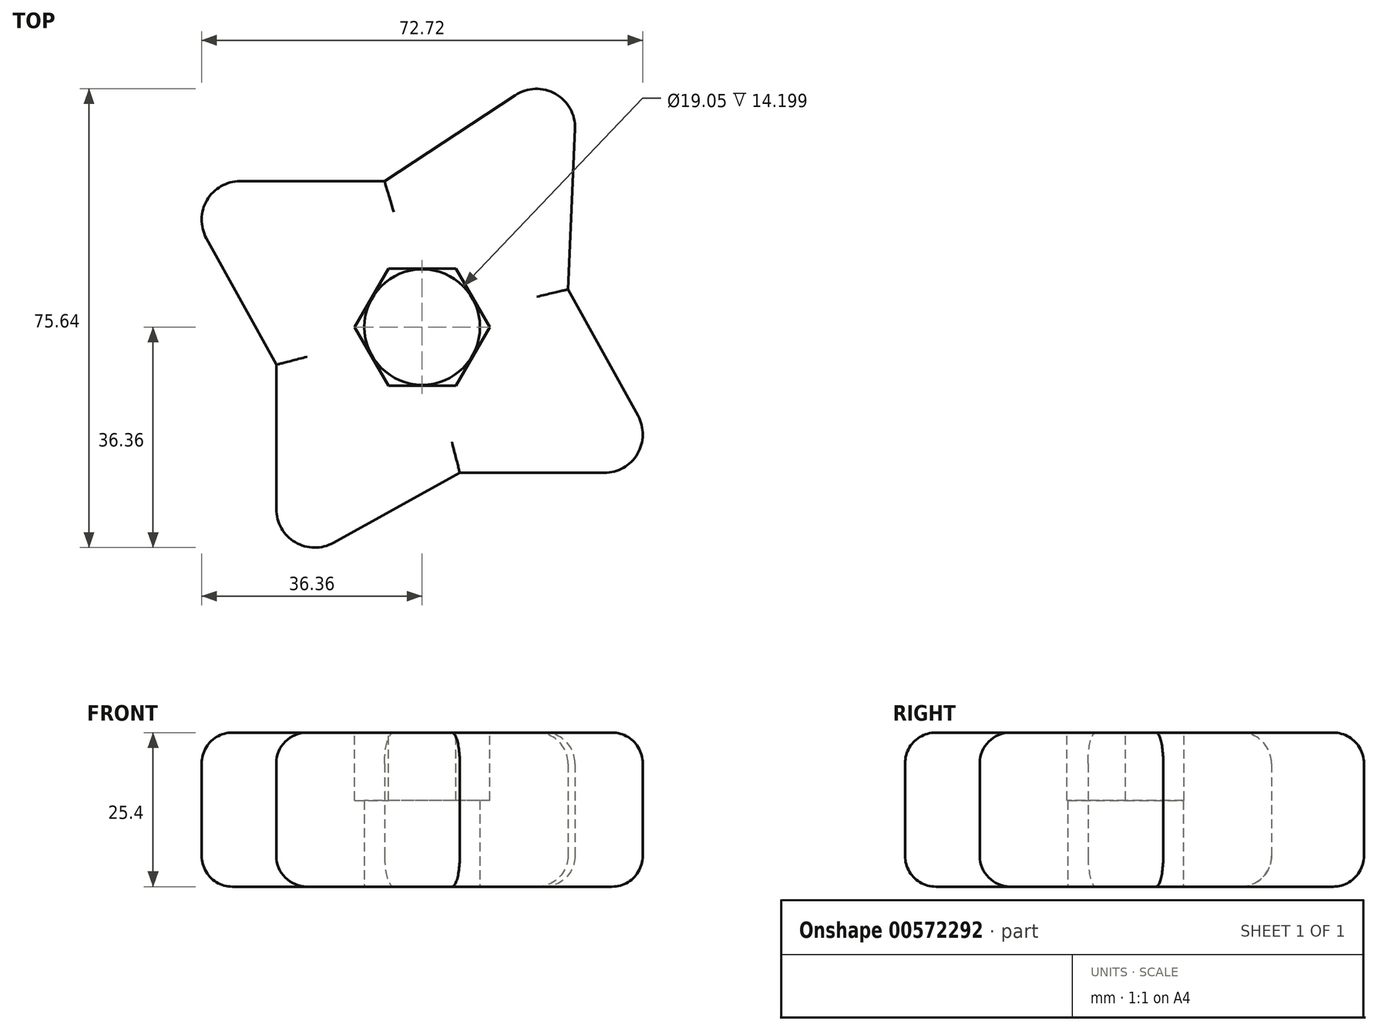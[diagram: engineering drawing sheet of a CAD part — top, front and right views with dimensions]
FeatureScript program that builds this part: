
annotation { "Feature Type Name" : "Feature", "Feature Type Description" : "" }
export const myFeature = defineFeature(function(context is Context, id is Id, definition is map)
    precondition{}
    {
        {
            var Q0;
            Q0=qCreatedBy(makeId("Top.planeOp"),FACE);
            var sketch = newSketch(context, id + "F0", { "sketchPlane" : qUnion([Q0])});
            skCircle(sketch, "E0.cCircle", {"center": v(0, 0) * mm, "radius": 17.56 * mm, "construction": true});
            skLineSegment(sketch, "E1", {"start": v(-6.2, 24.05) * mm, "end": v(15.35, 38.23) * mm});
            skLineSegment(sketch, "E2", {"start": v(25.18, 32.65) * mm, "end": v(24.05, 6.2) * mm});
            skLineSegment(sketch, "E3", {"start": v(-24.05, -6.2) * mm, "end": v(-24.05, -30) * mm});
            skLineSegment(sketch, "E4", {"start": v(6.2, -24.05) * mm, "end": v(-14.62, -35.56) * mm});
            skLineSegment(sketch, "E5", {"start": v(24.05, 6.2) * mm, "end": v(35.56, -14.62) * mm});
            skLineSegment(sketch, "E6", {"start": v(30, -24.05) * mm, "end": v(6.2, -24.05) * mm});
            skLineSegment(sketch, "E7", {"start": v(-24.05, -6.2) * mm, "end": v(-35.56, 14.62) * mm});
            skLineSegment(sketch, "E8", {"start": v(-30, 24.05) * mm, "end": v(-6.2, 24.05) * mm});
            skArc(sketch, "E9.filletArc", {"start": v(25.18, 32.65) * mm, "mid": v(21.97, 38.45) * mm, "end": v(15.35, 38.23) * mm});
            skArc(sketch, "E10.filletArc", {"start": v(30, -24.05) * mm, "mid": v(35.48, -20.92) * mm, "end": v(35.56, -14.62) * mm});
            skArc(sketch, "E11.filletArc", {"start": v(-24.05, -30) * mm, "mid": v(-20.92, -35.48) * mm, "end": v(-14.62, -35.56) * mm});
            skArc(sketch, "E12.filletArc", {"start": v(-30, 24.05) * mm, "mid": v(-35.48, 20.92) * mm, "end": v(-35.56, 14.62) * mm});
            skCircle(sketch, "E13", {"center": v(0, 0) * mm, "radius": 9.53 * mm});
            skSolve(sketch);
        }
        {
            var Q0;
            Q0=makeQuery(id+"F0.imprint","IMPRINT",FACE,{"disambiguationData":[TD([[makeQuery(id+"F0.imprint","IMPRINT",EDGE,{"derivedFrom":sQuery(id+"F0.wireOp",EDGE,"E1")}),-1.0]])]});
            extrude(context, id + "F1", {"entities" : qUnion([Q0]), "depth" : 25.4 * mm, "offsetDistance" : 25.4 * mm});
        }
        {
            var Q0;
            Q0=makeQuery(id+"F1.opExtrude","CAP_EDGE",EDGE,{"disambiguationData":[OSD([sQuery(id+"F0.wireOp",EDGE,"E7")])],"isStart":true});
            var Q1;
            Q1=makeQuery(id+"F1.opExtrude","CAP_EDGE",EDGE,{"disambiguationData":[OSD([sQuery(id+"F0.wireOp",EDGE,"E1")])],"isStart":true});
            fillet(context, id + "F2", {"entities" : qUnion([Q0, Q1]), "radius" : 5.08 * mm, "tangentPropagation" : true, "allowEdgeOverflow" : false});
        }
        {
            var Q0;
            Q0=makeQuery(id+"F1.opExtrude","CAP_EDGE",EDGE,{"disambiguationData":[OSD([sQuery(id+"F0.wireOp",EDGE,"E3")])],"isStart":true});
            var Q1;
            Q1=makeQuery(id+"F1.opExtrude","CAP_EDGE",EDGE,{"disambiguationData":[OSD([sQuery(id+"F0.wireOp",EDGE,"E1")])],"isStart":false});
            var Q2;
            Q2=makeQuery(id+"F1.opExtrude","CAP_EDGE",EDGE,{"disambiguationData":[OSD([sQuery(id+"F0.wireOp",EDGE,"E8")])],"isStart":false});
            var Q3;
            Q3=makeQuery(id+"F1.opExtrude","CAP_EDGE",EDGE,{"disambiguationData":[OSD([sQuery(id+"F0.wireOp",EDGE,"E3")])],"isStart":false});
            var Q4;
            Q4=makeQuery(id+"F1.opExtrude","CAP_EDGE",EDGE,{"disambiguationData":[OSD([sQuery(id+"F0.wireOp",EDGE,"E6")])],"isStart":false});
            var Q5;
            Q5=makeQuery(id+"F1.opExtrude","CAP_EDGE",EDGE,{"disambiguationData":[OSD([sQuery(id+"F0.wireOp",EDGE,"E6")])],"isStart":true});
            fillet(context, id + "F3", {"entities" : qUnion([Q0, Q1, Q2, Q3, Q4, Q5]), "radius" : 5.08 * mm, "tangentPropagation" : true, "allowEdgeOverflow" : false});
        }
        {
            var Q0;
            Q0=makeQuery(id+"F1.opExtrude","CAP_FACE",FACE,{"disambiguationData":[OSD([sQuery(id+"F0.wireOp",EDGE,"E1"),sQuery(id+"F0.wireOp",EDGE,"E2"),sQuery(id+"F0.wireOp",EDGE,"E3"),sQuery(id+"F0.wireOp",EDGE,"E4"),sQuery(id+"F0.wireOp",EDGE,"E5"),sQuery(id+"F0.wireOp",EDGE,"E6"),sQuery(id+"F0.wireOp",EDGE,"E7"),sQuery(id+"F0.wireOp",EDGE,"E8"),sQuery(id+"F0.wireOp",EDGE,"E9.filletArc"),sQuery(id+"F0.wireOp",EDGE,"E10.filletArc"),sQuery(id+"F0.wireOp",EDGE,"E11.filletArc"),sQuery(id+"F0.wireOp",EDGE,"E12.filletArc"),sQuery(id+"F0.wireOp",EDGE,"E13")])],"isStart":false});
            var sketch = newSketch(context, id + "F4", { "sketchPlane" : qUnion([Q0])});
            skCircle(sketch, "E14.cCircle", {"center": v(0, 0) * mm, "radius": 9.65 * mm, "construction": true});
            skLineSegment(sketch, "E14.0", {"start": v(5.57, -9.65) * mm, "end": v(-5.57, -9.65) * mm});
            skLineSegment(sketch, "E14.1", {"start": v(-5.57, -9.65) * mm, "end": v(-11.15, 0) * mm});
            skLineSegment(sketch, "E14.2", {"start": v(-11.15, 0) * mm, "end": v(-5.57, 9.65) * mm});
            skLineSegment(sketch, "E14.3", {"start": v(-5.57, 9.65) * mm, "end": v(5.57, 9.65) * mm});
            skLineSegment(sketch, "E14.4", {"start": v(5.57, 9.65) * mm, "end": v(11.15, 0) * mm});
            skLineSegment(sketch, "E14.5", {"start": v(11.15, 0) * mm, "end": v(5.57, -9.65) * mm});
            skPoint(sketch, "E14.0.midPoint", {"position": v(0, -9.65) * mm});
            skSolve(sketch);
        }
        {
            var Q0;
            Q0 = qSketchRegion(id + "F4", true);
            extrude(context, id + "F5", {"entities" : qUnion([Q0]), "operationType" : NewBodyOperationType.REMOVE, "oppositeDirection" : true, "depth" : 11.2 * mm, "offsetDistance" : 25.4 * mm});
        }
    });
